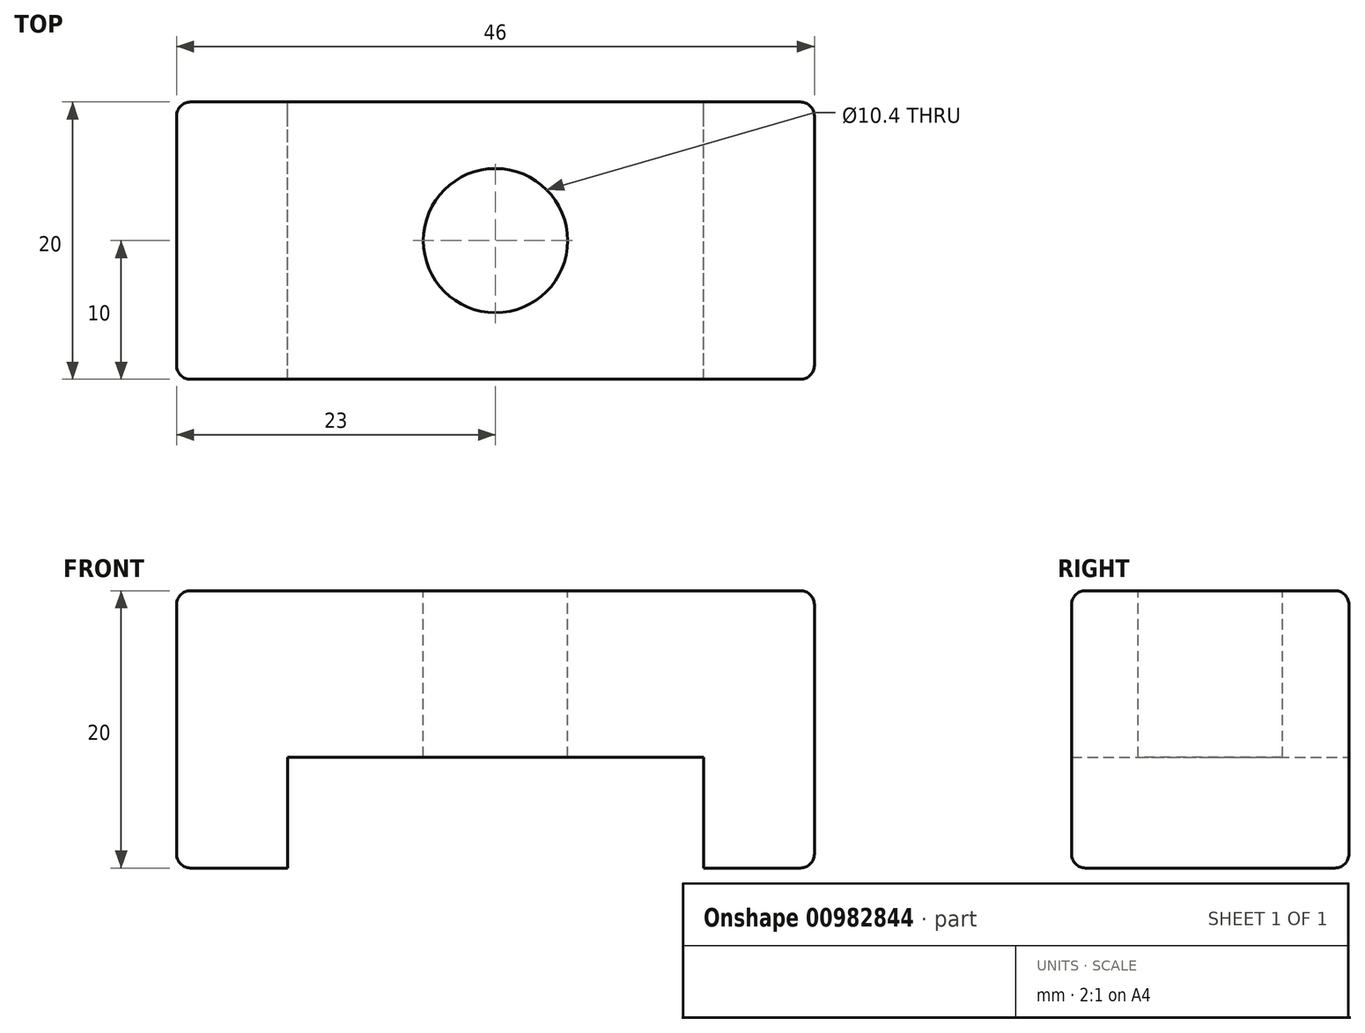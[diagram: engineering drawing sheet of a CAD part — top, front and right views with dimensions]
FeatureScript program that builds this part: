
annotation { "Feature Type Name" : "Feature", "Feature Type Description" : "" }
export const myFeature = defineFeature(function(context is Context, id is Id, definition is map)
    precondition{}
    {
        {
            var Q0;
            Q0=qCreatedBy(makeId("Front.planeOp"),FACE);
            var sketch = newSketch(context, id + "F0", { "sketchPlane" : qUnion([Q0])});
            skLineSegment(sketch, "E0.top", {"start": v(-22, 10) * mm, "end": v(22, 10) * mm});
            skLineSegment(sketch, "E0.left", {"start": v(-23, -9) * mm, "end": v(-23, 9) * mm});
            skLineSegment(sketch, "E0.right", {"start": v(23, -9) * mm, "end": v(23, 9) * mm});
            skPoint(sketch, "E0.middle", {"position": v(0, 0) * mm});
            skLineSegment(sketch, "E1", {"start": v(15, -2) * mm, "end": v(15, -10) * mm});
            skLineSegment(sketch, "E2", {"start": v(-22, -10) * mm, "end": v(-15, -10) * mm});
            skLineSegment(sketch, "E3", {"start": v(-15, -2) * mm, "end": v(-15, -10) * mm});
            skPoint(sketch, "E4.trimOffspring.start.orphan", {"position": v(15, -15.42) * mm});
            skLineSegment(sketch, "E5.trimOffspring", {"start": v(-15, -2) * mm, "end": v(15, -2) * mm});
            skLineSegment(sketch, "E6.trimOffspring", {"start": v(15, -10) * mm, "end": v(22, -10) * mm});
            skPoint(sketch, "E7.visualSharp", {"position": v(-23, 10) * mm});
            skArc(sketch, "E7.filletArc", {"start": v(-22, 10) * mm, "mid": v(-22.7, 9.7) * mm, "end": v(-23, 9) * mm});
            skPoint(sketch, "E8.visualSharp", {"position": v(23, 10) * mm});
            skArc(sketch, "E8.filletArc", {"start": v(23, 9) * mm, "mid": v(22.7, 9.7) * mm, "end": v(22, 10) * mm});
            skPoint(sketch, "E9.visualSharp", {"position": v(23, -10) * mm});
            skArc(sketch, "E9.filletArc", {"start": v(22, -10) * mm, "mid": v(22.7, -9.7) * mm, "end": v(23, -9) * mm});
            skPoint(sketch, "E10.visualSharp", {"position": v(-23, -10) * mm});
            skArc(sketch, "E10.filletArc", {"start": v(-23, -9) * mm, "mid": v(-22.7, -9.7) * mm, "end": v(-22, -10) * mm});
            skSolve(sketch);
        }
        {
            var Q0;
            Q0 = qSketchRegion(id + "F0", true);
            extrude(context, id + "F1", {"entities" : qUnion([Q0]), "depth" : 20 * mm, "offsetDistance" : 25 * mm});
        }
        {
            var Q0;
            Q0=makeQuery(id+"F1.opExtrude","SWEPT_FACE",FACE,{"disambiguationData":[OSD([sQuery(id+"F0.wireOp",EDGE,"E0.top")])]});
            var sketch = newSketch(context, id + "F2", { "sketchPlane" : qUnion([Q0])});
            skCircle(sketch, "E11", {"center": v(0, -10) * mm, "radius": 5.2 * mm});
            skSolve(sketch);
        }
        {
            var Q0;
            Q0=makeQuery(id+"F2.imprint","IMPRINT",FACE,{"disambiguationData":[TD([[makeQuery(id+"F2.imprint","IMPRINT",EDGE,{"derivedFrom":sQuery(id+"F2.wireOp",EDGE,"E11")}),1.0]])]});
            extrude(context, id + "F3", {"entities" : qUnion([Q0]), "operationType" : NewBodyOperationType.REMOVE, "oppositeDirection" : true, "depth" : 25 * mm, "offsetDistance" : 25 * mm});
        }
        {
            var Q0;
            Q0=makeQuery(id+"F1.opExtrude","CAP_EDGE",EDGE,{"disambiguationData":[OSD([sQuery(id+"F0.wireOp",EDGE,"E0.top")])],"isStart":false});
            var Q1;
            Q1=makeQuery(id+"F1.opExtrude","CAP_EDGE",EDGE,{"disambiguationData":[OSD([sQuery(id+"F0.wireOp",EDGE,"E0.right")])],"isStart":false});
            var Q2;
            Q2=makeQuery(id+"F1.opExtrude","CAP_EDGE",EDGE,{"disambiguationData":[OSD([sQuery(id+"F0.wireOp",EDGE,"E0.top")])],"isStart":true});
            var Q3;
            Q3=makeQuery(id+"F1.opExtrude","CAP_EDGE",EDGE,{"disambiguationData":[OSD([sQuery(id+"F0.wireOp",EDGE,"E0.right")])],"isStart":true});
            fillet(context, id + "F4", {"entities" : qUnion([Q0, Q1, Q2, Q3]), "radius" : 1 * mm, "tangentPropagation" : true, "allowEdgeOverflow" : false});
        }
    });
